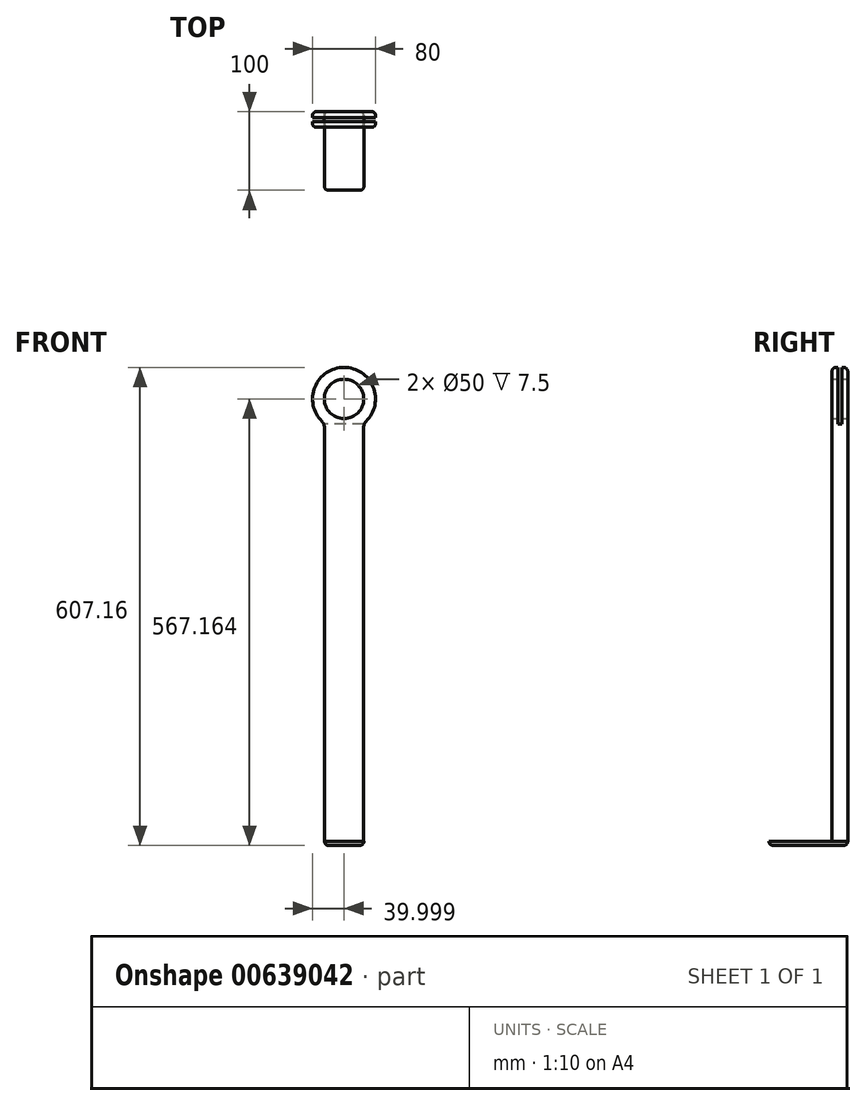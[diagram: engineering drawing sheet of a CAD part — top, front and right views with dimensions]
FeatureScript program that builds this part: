
annotation { "Feature Type Name" : "Feature", "Feature Type Description" : "" }
export const myFeature = defineFeature(function(context is Context, id is Id, definition is map)
    precondition{}
    {
        {
            var Q0;
            Q0=qCreatedBy(makeId("Front.planeOp"),FACE);
            var sketch = newSketch(context, id + "F0", { "sketchPlane" : qUnion([Q0])});
            skLineSegment(sketch, "E0", {"start": v(-85.5, -86.41) * mm, "end": v(-25.2, -86.41) * mm, "construction": true});
            skLineSegment(sketch, "E1", {"start": v(-0.2, -86.41) * mm, "end": v(-0.2, 435.75) * mm, "construction": true});
            skLineSegment(sketch, "E2", {"start": v(-25.2, -86.41) * mm, "end": v(-25.2, 440.05) * mm});
            skLineSegment(sketch, "E3", {"start": v(24.8, -86.41) * mm, "end": v(24.8, 440.05) * mm});
            skArc(sketch, "E4", {"start": v(27.8, 447.19) * mm, "mid": v(-0.2, 515.75) * mm, "end": v(-28.2, 447.19) * mm});
            skLineSegment(sketch, "E5.trimOffspring", {"start": v(24.8, -86.41) * mm, "end": v(85.11, -86.41) * mm, "construction": true});
            skLineSegment(sketch, "E6", {"start": v(-25.2, -86.41) * mm, "end": v(24.8, -86.41) * mm});
            skPoint(sketch, "E7.visualSharp", {"position": v(-25.2, 444.53) * mm});
            skArc(sketch, "E7.filletArc", {"start": v(-25.2, 440.05) * mm, "mid": v(-25.97, 443.92) * mm, "end": v(-28.2, 447.19) * mm});
            skPoint(sketch, "E8.visualSharp", {"position": v(24.8, 444.53) * mm});
            skArc(sketch, "E8.filletArc", {"start": v(27.8, 447.19) * mm, "mid": v(25.59, 443.92) * mm, "end": v(24.8, 440.05) * mm});
            skCircle(sketch, "E9", {"center": v(-0.2, 475.75) * mm, "radius": 25 * mm});
            skSolve(sketch);
        }
        {
            var Q0;
            Q0=makeQuery(id+"F0.imprint","IMPRINT",FACE,{"disambiguationData":[TD([[makeQuery(id+"F0.imprint","IMPRINT",EDGE,{"derivedFrom":sQuery(id+"F0.wireOp",EDGE,"E2")}),-1.0]])]});
            extrude(context, id + "F1", {"entities" : qUnion([Q0]), "depth" : 20 * mm, "offsetDistance" : 25 * mm});
        }
        {
            var Q0;
            Q0=makeQuery(id+"F1.opExtrude","SWEPT_FACE",FACE,{"disambiguationData":[OSD([sQuery(id+"F0.wireOp",EDGE,"E2")])]});
            var sketch = newSketch(context, id + "F2", { "sketchPlane" : qUnion([Q0])});
            skLineSegment(sketch, "E10.0", {"start": v(20, 500.75) * mm, "end": v(20, 450.75) * mm});
            skLineSegment(sketch, "E11.0", {"start": v(0, 500.75) * mm, "end": v(0, 450.75) * mm});
            skLineSegment(sketch, "E12.0", {"start": v(0, 447.19) * mm, "end": v(0, 515.75) * mm});
            skLineSegment(sketch, "E13.0", {"start": v(20, 447.19) * mm, "end": v(20, 515.75) * mm});
            skLineSegment(sketch, "E14", {"start": v(0, 515.75) * mm, "end": v(20, 515.75) * mm});
            skLineSegment(sketch, "E15", {"start": v(0, 450.75) * mm, "end": v(7.5, 450.75) * mm});
            skLineSegment(sketch, "E16", {"start": v(10, 515.75) * mm, "end": v(10, 450.75) * mm, "construction": true});
            skLineSegment(sketch, "E17", {"start": v(7.5, 443.62) * mm, "end": v(7.5, 515.75) * mm});
            skLineSegment(sketch, "E18", {"start": v(12.5, 515.75) * mm, "end": v(12.5, 443.62) * mm});
            skLineSegment(sketch, "E19.0", {"start": v(20, 447.19) * mm, "end": v(12.5, 447.19) * mm});
            skLineSegment(sketch, "E20.trimOffspring", {"start": v(12.5, 450.75) * mm, "end": v(20, 450.75) * mm});
            skLineSegment(sketch, "E21.0", {"start": v(0, 440.05) * mm, "end": v(0, 447.19) * mm});
            skLineSegment(sketch, "E22.0", {"start": v(20, 440.05) * mm, "end": v(20, 447.19) * mm});
            skLineSegment(sketch, "E23", {"start": v(0, 443.62) * mm, "end": v(20, 443.62) * mm});
            skLineSegment(sketch, "E24.trimOffspring", {"start": v(7.5, 447.19) * mm, "end": v(0, 447.19) * mm});
            skSolve(sketch);
        }
        {
            var Q0;
            {var subQ0=sQuery(id+"F2.wireOp",EDGE,"E17");Q0=makeQuery(id+"F2.imprint","IMPRINT",FACE,{"disambiguationData":[TD([[makeQuery(id+"F2.imprint","IMPRINT",EDGE,{"derivedFrom":subQ0}),-1.0]])]});}
            extrude(context, id + "F3", {"entities" : qUnion([Q0]), "operationType" : NewBodyOperationType.REMOVE, "endBound" : BoundingType.SYMMETRIC, "oppositeDirection" : true, "depth" : 140 * mm, "offsetDistance" : 25 * mm});
        }
        {
            var Q0;
            Q0=makeQuery(id+"F1.opExtrude","CAP_EDGE",EDGE,{"disambiguationData":[OSD([sQuery(id+"F0.wireOp",EDGE,"E2")])],"isStart":false});
            var Q1;
            Q1=makeQuery(id+"F1.opExtrude","CAP_EDGE",EDGE,{"disambiguationData":[OSD([sQuery(id+"F0.wireOp",EDGE,"E2")])],"isStart":true});
            fillet(context, id + "F4", {"entities" : qUnion([Q0, Q1]), "radius" : 5 * mm, "tangentPropagation" : true, "allowEdgeOverflow" : false});
        }
        {
            var Q0;
            Q0=qCreatedBy(makeId("Right.planeOp"),FACE);
            var sketch = newSketch(context, id + "F5", { "sketchPlane" : qUnion([Q0])});
            skLineSegment(sketch, "E25.0", {"start": v(0, -86.41) * mm, "end": v(0, 440.05) * mm});
            skLineSegment(sketch, "E26.0", {"start": v(-20, 440.05) * mm, "end": v(-20, -86.41) * mm});
            skLineSegment(sketch, "E27.bottom", {"start": v(0, -86.41) * mm, "end": v(-100, -86.41) * mm});
            skLineSegment(sketch, "E27.top", {"start": v(0, -91.41) * mm, "end": v(-100, -91.41) * mm});
            skLineSegment(sketch, "E27.left", {"start": v(0, -86.41) * mm, "end": v(0, -91.41) * mm});
            skLineSegment(sketch, "E27.right", {"start": v(-100, -86.41) * mm, "end": v(-100, -91.41) * mm});
            skSolve(sketch);
        }
        {
            var Q0;
            Q0=makeQuery(id+"F5.imprint","IMPRINT",FACE,{"disambiguationData":[TD([[makeQuery(id+"F5.imprint","IMPRINT",EDGE,{"derivedFrom":sQuery(id+"F5.wireOp",EDGE,"E27.top")}),-1.0]])]});
            extrude(context, id + "F6", {"entities" : qUnion([Q0]), "operationType" : NewBodyOperationType.ADD, "endBound" : BoundingType.SYMMETRIC, "depth" : 50 * mm, "offsetDistance" : 25 * mm});
        }
        {
            var Q0;
            Q0=makeQuery(id+"F6.opExtrude","CAP_EDGE",EDGE,{"disambiguationData":[OSD([sQuery(id+"F5.wireOp",EDGE,"E27.left")])],"isStart":true});
            var Q1;
            Q1=makeQuery(id+"F6.opExtrude","CAP_EDGE",EDGE,{"disambiguationData":[OSD([sQuery(id+"F5.wireOp",EDGE,"E27.left")])],"isStart":false});
            var Q2;
            Q2=makeQuery(id+"F6.opExtrude","CAP_EDGE",EDGE,{"disambiguationData":[OSD([sQuery(id+"F5.wireOp",EDGE,"E27.right")])],"isStart":true});
            var Q3;
            Q3=makeQuery(id+"F6.opExtrude","CAP_EDGE",EDGE,{"disambiguationData":[OSD([sQuery(id+"F5.wireOp",EDGE,"E27.right")])],"isStart":false});
            fillet(context, id + "F7", {"entities" : qUnion([Q0, Q1, Q2, Q3]), "radius" : 5 * mm, "tangentPropagation" : true, "allowEdgeOverflow" : false});
        }
        {
            var Q0;
            Q0=makeQuery(id+"F6.opExtrude","SWEPT_FACE",FACE,{"disambiguationData":[OSD([sQuery(id+"F5.wireOp",EDGE,"E27.top")])]});
            fillet(context, id + "F8", {"entities" : qUnion([Q0]), "radius" : 5 * mm, "tangentPropagation" : true, "allowEdgeOverflow" : false});
        }
    });
